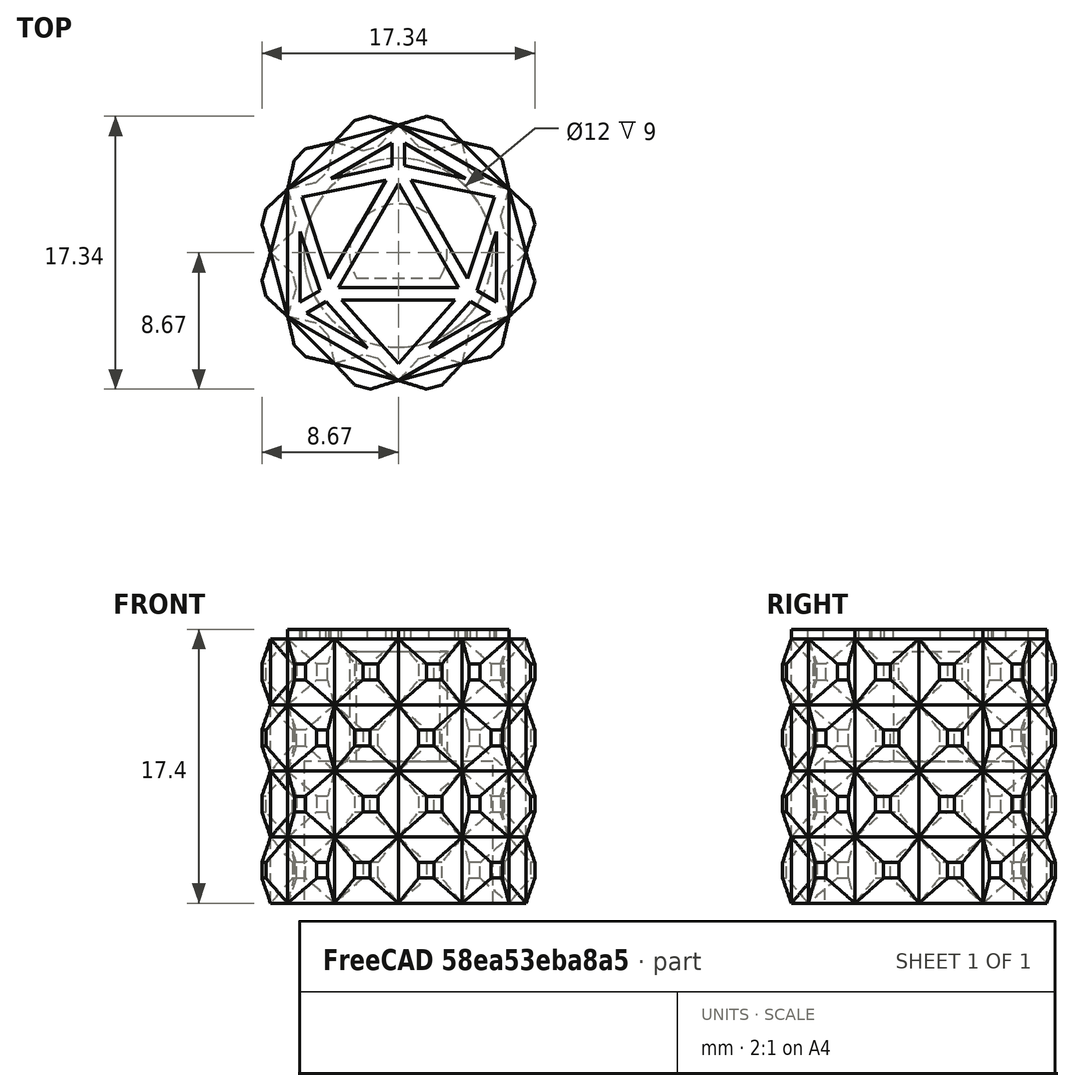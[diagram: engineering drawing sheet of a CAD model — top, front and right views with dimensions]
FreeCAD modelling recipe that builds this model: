
FCSTD DOCUMENT  (FreeCAD 1.0R38641 +678 (Git))
Label: knob
License: All rights reserved
LicenseURL: https://en.wikipedia.org/wiki/All_rights_reserved
objects: Sketcher::SketchObject×18, PartDesign::Pad×5, PartDesign::Pocket×5, PartDesign::AdditiveLoft×2, PartDesign::SubtractiveLoft×2, PartDesign::PolarPattern×1, PartDesign::LinearPattern×1, PartDesign::MultiTransform×1, PartDesign::Body×1, Mesh::Feature×1
note: 85 computed .brp shape members not serialized (recipe doc carries the construction recipe); baked Part::Feature solids carry a one-line shape summary decoded from their .brp

FEATURE [Sketcher::SketchObject] Sketch
  ArcFitTolerance = 0
  AttachmentSupport = -> [XY_Plane]
  FullyConstrained = true
  MakeInternals = false
  MapMode = 5
  sketch-geometry (5):
    g0: LineSegment StartX=0 StartY=0 StartZ=0 EndX=0 EndY=-8.11378 EndZ=0
    g1: LineSegment [constr] StartX=0 StartY=0 StartZ=0 EndX=4.05689 EndY=-7.02674 EndZ=0
    g2: LineSegment StartX=0 StartY=-8.11378 StartZ=0 EndX=4.05689 EndY=-7.02674 EndZ=0
    g3: LineSegment StartX=0 StartY=0 StartZ=0 EndX=7.02674 EndY=-4.05689 EndZ=0
    g4: LineSegment StartX=4.05689 StartY=-7.02674 StartZ=0 EndX=7.02674 EndY=-4.05689 EndZ=0
  constraints (13):
    c: Coincident(g0,g-1)
    c: PointOnObject(g0,g-2)
    c: Coincident(g1,g0)
    c: Equal(g0,g1)
    c: Coincident(g2,g0)
    c: Coincident(g1,g2)
    c: Angle(g0,g1) = 0.523599
    c: Coincident(g3,g0)
    c: Coincident(g4,g1)
    c: Coincident(g4,g3)
    c: Equal(g1,g3)
    c: Angle(g1,g3) = 0.523599
    c: Distance(g2) = 4.2
FEATURE [PartDesign::Pad] Pad
  Direction = (0,0,1)
  Length = 8.4
  Length2 = 10
  Profile = -> Sketch
  ReferenceAxis = -> Sketch [N_Axis]
  Suppressed = false
  Type = 0
FEATURE [Sketcher::SketchObject] Sketch001
  ArcFitTolerance = 0
  AttachmentSupport = -> [Pad]
  ExternalGeometry = -> [Pad]
  FullyConstrained = true
  MakeInternals = false
  MapMode = 5
  Placement = pos=(2.02844,-7.57026,0) rot=(0.983106,0.129428,0.129428;1.58783rad)
  sketch-geometry (4):
    g0: LineSegment StartX=-0.5 StartY=6.8 StartZ=0 EndX=0.5 EndY=6.8 EndZ=0
    g1: LineSegment StartX=0.5 StartY=6.8 StartZ=0 EndX=0.5 EndY=5.8 EndZ=0
    g2: LineSegment StartX=0.5 StartY=5.8 StartZ=0 EndX=-0.5 EndY=5.8 EndZ=0
    g3: LineSegment StartX=-0.5 StartY=5.8 StartZ=0 EndX=-0.5 EndY=6.8 EndZ=0
  constraints (12):
    c: Coincident(g0,g1)
    c: Coincident(g1,g2)
    c: Coincident(g2,g3)
    c: Coincident(g3,g0)
    c: Horizontal(g0)
    c: Horizontal(g2)
    c: Vertical(g1)
    c: Vertical(g3)
    c: DistanceX(g-4,g0) = 1.6
    c: DistanceX(g0,g-5) = 1.6
    c: DistanceY(g0,g-4) = 1.6
    c: DistanceY(g3,g3) = 1
FEATURE [PartDesign::Pad] Pad001
  BaseFeature = -> Pad
  Direction = (0.258819,-0.965926,0)
  Length = 1
  Length2 = 10
  Profile = -> Sketch001
  ReferenceAxis = -> Sketch001 [N_Axis]
  Suppressed = false
  Type = 0
FEATURE [Sketcher::SketchObject] Sketch002
  ArcFitTolerance = 0
  AttachmentSupport = -> [Pad001]
  ExternalGeometry = -> [Pad001]
  FullyConstrained = true
  MakeInternals = false
  MapMode = 5
  Placement = pos=(2.02844,-7.57026,0) rot=(0.983106,0.129428,0.129428;1.58783rad)
  sketch-geometry (4):
    g0: LineSegment StartX=-2.1 StartY=8.4 StartZ=0 EndX=2.1 EndY=8.4 EndZ=0
    g1: LineSegment StartX=2.1 StartY=8.4 StartZ=0 EndX=2.1 EndY=4.2 EndZ=0
    g2: LineSegment StartX=2.1 StartY=4.2 StartZ=0 EndX=-2.1 EndY=4.2 EndZ=0
    g3: LineSegment StartX=-2.1 StartY=4.2 StartZ=0 EndX=-2.1 EndY=8.4 EndZ=0
  constraints (10):
    c: Coincident(g0,g1)
    c: Coincident(g1,g2)
    c: Coincident(g2,g3)
    c: Coincident(g3,g0)
    c: Horizontal(g2)
    c: Vertical(g1)
    c: Vertical(g3)
    c: DistanceY(g3,g3) = 4.2
    c: Coincident(g0,g-5)
    c: Coincident(g0,g-4)
FEATURE [Sketcher::SketchObject] Sketch003
  ArcFitTolerance = 0
  AttachmentSupport = -> [Pad001]
  ExternalGeometry = -> [Pad001]
  FullyConstrained = true
  MakeInternals = false
  MapMode = 5
  Placement = pos=(2.28726,-8.53618,0) rot=(0.983106,0.129428,0.129428;1.58783rad)
  sketch-geometry (4):
    g0: LineSegment StartX=-0.5 StartY=6.8 StartZ=0 EndX=0.5 EndY=6.8 EndZ=0
    g1: LineSegment StartX=0.5 StartY=6.8 StartZ=0 EndX=0.5 EndY=5.8 EndZ=0
    g2: LineSegment StartX=0.5 StartY=5.8 StartZ=0 EndX=-0.5 EndY=5.8 EndZ=0
    g3: LineSegment StartX=-0.5 StartY=5.8 StartZ=0 EndX=-0.5 EndY=6.8 EndZ=0
  constraints (10):
    c: Coincident(g0,g1)
    c: Coincident(g1,g2)
    c: Coincident(g2,g3)
    c: Coincident(g3,g0)
    c: Horizontal(g0)
    c: Horizontal(g2)
    c: Vertical(g1)
    c: Vertical(g3)
    c: Coincident(g0,g-6)
    c: Coincident(g1,g-5)
FEATURE [PartDesign::AdditiveLoft] AdditiveLoft
  BaseFeature = -> Pad001
  Closed = false
  Profile = -> Sketch002
  Ruled = false
  Sections = -> [Sketch003]
  Suppressed = false
FEATURE [Sketcher::SketchObject] Sketch004
  ArcFitTolerance = 0
  AttachmentSupport = -> [AdditiveLoft]
  ExternalGeometry = -> [AdditiveLoft]
  FullyConstrained = true
  MakeInternals = false
  MapMode = 5
  Placement = pos=(2.02844,-7.57026,0) rot=(0.983106,0.129428,0.129428;1.58783rad)
  sketch-geometry (4):
    g0: LineSegment StartX=-0.5 StartY=2.6 StartZ=0 EndX=0.5 EndY=2.6 EndZ=0
    g1: LineSegment StartX=0.5 StartY=2.6 StartZ=0 EndX=0.5 EndY=1.6 EndZ=0
    g2: LineSegment StartX=0.5 StartY=1.6 StartZ=0 EndX=-0.5 EndY=1.6 EndZ=0
    g3: LineSegment StartX=-0.5 StartY=1.6 StartZ=0 EndX=-0.5 EndY=2.6 EndZ=0
  constraints (12):
    c: Coincident(g0,g1)
    c: Coincident(g1,g2)
    c: Coincident(g2,g3)
    c: Coincident(g3,g0)
    c: Horizontal(g0)
    c: Horizontal(g2)
    c: Vertical(g1)
    c: Vertical(g3)
    c: DistanceX(g-3,g2) = 1.6
    c: DistanceY(g-3,g2) = 1.6
    c: DistanceX(g1,g-4) = 1.6
    c: DistanceY(g3,g3) = 1
FEATURE [PartDesign::Pocket] Pocket
  BaseFeature = -> AdditiveLoft
  Direction = (-0.258819,0.965926,0)
  Length = 1
  Length2 = 5
  Profile = -> Sketch004
  ReferenceAxis = -> Sketch004 [N_Axis]
  Suppressed = false
  Type = 0
FEATURE [Sketcher::SketchObject] Sketch005
  ArcFitTolerance = 0
  AttachmentSupport = -> [Pocket]
  ExternalGeometry = -> [Pocket]
  FullyConstrained = true
  MakeInternals = false
  MapMode = 5
  Placement = pos=(2.02844,-7.57026,0) rot=(0.983106,0.129428,0.129428;1.58783rad)
  sketch-geometry (4):
    g0: LineSegment StartX=-2.1 StartY=4.2 StartZ=0 EndX=2.1 EndY=4.2 EndZ=0
    g1: LineSegment StartX=2.1 StartY=4.2 StartZ=0 EndX=2.1 EndY=0 EndZ=0
    g2: LineSegment StartX=2.1 StartY=0 StartZ=0 EndX=-2.1 EndY=0 EndZ=0
    g3: LineSegment StartX=-2.1 StartY=0 StartZ=0 EndX=-2.1 EndY=4.2 EndZ=0
  constraints (10):
    c: Coincident(g0,g1)
    c: Coincident(g1,g2)
    c: Coincident(g2,g3)
    c: Coincident(g3,g0)
    c: Horizontal(g0)
    c: Horizontal(g2)
    c: Vertical(g1)
    c: Vertical(g3)
    c: Coincident(g0,g-4)
    c: Coincident(g1,g-6)
FEATURE [Sketcher::SketchObject] Sketch006
  ArcFitTolerance = 0
  AttachmentSupport = -> [Pocket]
  ExternalGeometry = -> [Pocket]
  FullyConstrained = true
  MakeInternals = false
  MapMode = 5
  Placement = pos=(1.76963,-6.60433,0) rot=(0.983106,0.129428,0.129428;1.58783rad)
  sketch-geometry (4):
    g0: LineSegment StartX=-0.5 StartY=2.6 StartZ=0 EndX=0.5 EndY=2.6 EndZ=0
    g1: LineSegment StartX=0.5 StartY=2.6 StartZ=0 EndX=0.5 EndY=1.6 EndZ=0
    g2: LineSegment StartX=0.5 StartY=1.6 StartZ=0 EndX=-0.5 EndY=1.6 EndZ=0
    g3: LineSegment StartX=-0.5 StartY=1.6 StartZ=0 EndX=-0.5 EndY=2.6 EndZ=0
  constraints (10):
    c: Coincident(g0,g1)
    c: Coincident(g1,g2)
    c: Coincident(g2,g3)
    c: Coincident(g3,g0)
    c: Horizontal(g0)
    c: Horizontal(g2)
    c: Vertical(g1)
    c: Vertical(g3)
    c: Coincident(g0,g-4)
    c: Coincident(g1,g-6)
FEATURE [PartDesign::SubtractiveLoft] SubtractiveLoft
  BaseFeature = -> Pocket
  Closed = false
  Profile = -> Sketch006
  Ruled = false
  Sections = -> [Sketch005]
  Suppressed = false
FEATURE [Sketcher::SketchObject] Sketch007
  ArcFitTolerance = 0
  AttachmentSupport = -> [SubtractiveLoft]
  ExternalGeometry = -> [SubtractiveLoft]
  FullyConstrained = true
  MakeInternals = false
  MapMode = 5
  Placement = pos=(5.54181,-5.54181,0) rot=(0.862856,0.357407,0.357407;1.71777rad)
  sketch-geometry (4):
    g0: LineSegment StartX=-0.5 StartY=6.8 StartZ=0 EndX=0.5 EndY=6.8 EndZ=0
    g1: LineSegment StartX=0.5 StartY=6.8 StartZ=0 EndX=0.5 EndY=5.8 EndZ=0
    g2: LineSegment StartX=0.5 StartY=5.8 StartZ=0 EndX=-0.5 EndY=5.8 EndZ=0
    g3: LineSegment StartX=-0.5 StartY=5.8 StartZ=0 EndX=-0.5 EndY=6.8 EndZ=0
  constraints (12):
    c: Coincident(g0,g1)
    c: Coincident(g1,g2)
    c: Coincident(g2,g3)
    c: Coincident(g3,g0)
    c: Horizontal(g0)
    c: Horizontal(g2)
    c: Vertical(g1)
    c: Vertical(g3)
    c: DistanceX(g-4,g0) = 1.6
    c: DistanceX(g0,g-3) = 1.6
    c: DistanceY(g0,g-3) = 1.6
    c: DistanceY(g1,g1) = 1
FEATURE [PartDesign::Pocket] Pocket001
  BaseFeature = -> SubtractiveLoft
  Direction = (-0.707107,0.707107,1e-16)
  Length = 1
  Length2 = 5
  Profile = -> Sketch007
  ReferenceAxis = -> Sketch007 [N_Axis]
  Suppressed = false
  Type = 0
FEATURE [Sketcher::SketchObject] Sketch008
  ArcFitTolerance = 0
  AttachmentSupport = -> [Pocket001]
  ExternalGeometry = -> [Pocket001]
  FullyConstrained = true
  MakeInternals = false
  MapMode = 5
  Placement = pos=(5.54181,-5.54181,0) rot=(0.862856,0.357407,0.357407;1.71777rad)
  sketch-geometry (4):
    g0: LineSegment StartX=-2.1 StartY=8.4 StartZ=0 EndX=2.1 EndY=8.4 EndZ=0
    g1: LineSegment StartX=2.1 StartY=8.4 StartZ=0 EndX=2.1 EndY=4.2 EndZ=0
    g2: LineSegment StartX=2.1 StartY=4.2 StartZ=0 EndX=-2.1 EndY=4.2 EndZ=0
    g3: LineSegment StartX=-2.1 StartY=4.2 StartZ=0 EndX=-2.1 EndY=8.4 EndZ=0
  constraints (9):
    c: Coincident(g0,g1)
    c: Coincident(g1,g2)
    c: Coincident(g2,g3)
    c: Coincident(g3,g0)
    c: Horizontal(g2)
    c: Vertical(g1)
    c: Coincident(g0,g-4)
    c: Coincident(g2,g-3)
    c: Coincident(g-4,g0)
FEATURE [Sketcher::SketchObject] Sketch009
  ArcFitTolerance = 0
  AttachmentSupport = -> [Pocket001]
  ExternalGeometry = -> [Pocket001]
  FullyConstrained = true
  MakeInternals = false
  MapMode = 5
  Placement = pos=(4.83471,-4.83471,0) rot=(0.862856,0.357407,0.357407;1.71777rad)
  sketch-geometry (4):
    g0: LineSegment StartX=-0.5 StartY=6.8 StartZ=0 EndX=0.5 EndY=6.8 EndZ=0
    g1: LineSegment StartX=0.5 StartY=6.8 StartZ=0 EndX=0.5 EndY=5.8 EndZ=0
    g2: LineSegment StartX=0.5 StartY=5.8 StartZ=0 EndX=-0.5 EndY=5.8 EndZ=0
    g3: LineSegment StartX=-0.5 StartY=5.8 StartZ=0 EndX=-0.5 EndY=6.8 EndZ=0
  constraints (10):
    c: Coincident(g0,g1)
    c: Coincident(g1,g2)
    c: Coincident(g2,g3)
    c: Coincident(g3,g0)
    c: Horizontal(g0)
    c: Horizontal(g2)
    c: Vertical(g1)
    c: Vertical(g3)
    c: Coincident(g0,g-4)
    c: Coincident(g1,g-6)
FEATURE [PartDesign::SubtractiveLoft] SubtractiveLoft001
  BaseFeature = -> Pocket001
  Closed = false
  Profile = -> Sketch008
  Ruled = false
  Sections = -> [Sketch009]
  Suppressed = false
FEATURE [Sketcher::SketchObject] Sketch010
  ArcFitTolerance = 0
  AttachmentSupport = -> [SubtractiveLoft001]
  ExternalGeometry = -> [SubtractiveLoft001]
  FullyConstrained = true
  MakeInternals = false
  MapMode = 5
  Placement = pos=(5.54181,-5.54181,0) rot=(0.862856,0.357407,0.357407;1.71777rad)
  sketch-geometry (4):
    g0: LineSegment StartX=-0.5 StartY=2.6 StartZ=0 EndX=0.5 EndY=2.6 EndZ=0
    g1: LineSegment StartX=0.5 StartY=2.6 StartZ=0 EndX=0.5 EndY=1.6 EndZ=0
    g2: LineSegment StartX=0.5 StartY=1.6 StartZ=0 EndX=-0.5 EndY=1.6 EndZ=0
    g3: LineSegment StartX=-0.5 StartY=1.6 StartZ=0 EndX=-0.5 EndY=2.6 EndZ=0
  constraints (12):
    c: Coincident(g0,g1)
    c: Coincident(g1,g2)
    c: Coincident(g2,g3)
    c: Coincident(g3,g0)
    c: Horizontal(g0)
    c: Horizontal(g2)
    c: Vertical(g1)
    c: Vertical(g3)
    c: DistanceX(g-6,g2) = 1.6
    c: DistanceX(g1,g-6) = 1.6
    c: DistanceY(g-6,g1) = 1.6
    c: DistanceY(g1,g1) = 1
FEATURE [PartDesign::Pad] Pad002
  BaseFeature = -> SubtractiveLoft001
  Direction = (0.707107,-0.707107,-1e-16)
  Length = 1
  Length2 = 10
  Profile = -> Sketch010
  ReferenceAxis = -> Sketch010 [N_Axis]
  Suppressed = false
  Type = 0
FEATURE [Sketcher::SketchObject] Sketch011
  ArcFitTolerance = 0
  AttachmentSupport = -> [Pad002]
  ExternalGeometry = -> [Pad002]
  FullyConstrained = true
  MakeInternals = false
  MapMode = 5
  Placement = pos=(5.54181,-5.54181,0) rot=(0.862856,0.357407,0.357407;1.71777rad)
  sketch-geometry (4):
    g0: LineSegment StartX=-2.1 StartY=4.2 StartZ=0 EndX=2.1 EndY=4.2 EndZ=0
    g1: LineSegment StartX=2.1 StartY=4.2 StartZ=0 EndX=2.1 EndY=0 EndZ=0
    g2: LineSegment StartX=2.1 StartY=0 StartZ=0 EndX=-2.1 EndY=0 EndZ=0
    g3: LineSegment StartX=-2.1 StartY=0 StartZ=0 EndX=-2.1 EndY=4.2 EndZ=0
  constraints (10):
    c: Coincident(g0,g1)
    c: Coincident(g1,g2)
    c: Coincident(g2,g3)
    c: Coincident(g3,g0)
    c: Horizontal(g0)
    c: Horizontal(g2)
    c: Vertical(g1)
    c: Vertical(g3)
    c: Coincident(g0,g-4)
    c: Coincident(g1,g-6)
FEATURE [Sketcher::SketchObject] Sketch012
  ArcFitTolerance = 0
  AttachmentSupport = -> [Pad002]
  ExternalGeometry = -> [Pad002]
  FullyConstrained = true
  MakeInternals = false
  MapMode = 5
  Placement = pos=(6.24892,-6.24892,-2.7e-15) rot=(0.862856,0.357407,0.357407;1.71777rad)
  sketch-geometry (4):
    g0: LineSegment StartX=-0.5 StartY=2.6 StartZ=0 EndX=0.5 EndY=2.6 EndZ=0
    g1: LineSegment StartX=0.5 StartY=2.6 StartZ=0 EndX=0.5 EndY=1.6 EndZ=0
    g2: LineSegment StartX=0.5 StartY=1.6 StartZ=0 EndX=-0.5 EndY=1.6 EndZ=0
    g3: LineSegment StartX=-0.5 StartY=1.6 StartZ=0 EndX=-0.5 EndY=2.6 EndZ=0
  constraints (10):
    c: Coincident(g0,g1)
    c: Coincident(g1,g2)
    c: Coincident(g2,g3)
    c: Coincident(g3,g0)
    c: Horizontal(g0)
    c: Horizontal(g2)
    c: Vertical(g1)
    c: Vertical(g3)
    c: Coincident(g0,g-4)
    c: Coincident(g1,g-6)
FEATURE [PartDesign::AdditiveLoft] AdditiveLoft001
  BaseFeature = -> Pad002
  Closed = false
  Profile = -> Sketch011
  Ruled = false
  Sections = -> [Sketch012]
  Suppressed = false
FEATURE [PartDesign::PolarPattern] PolarPattern
  Angle = 360
  Axis = -> Sketch [N_Axis]
  Mode = 0
  Occurrences = 6
  Offset = 120
  Suppressed = false
  TransformMode = 0
FEATURE [PartDesign::LinearPattern] LinearPattern
  Direction = -> Z_Axis
  Length = 8.4
  Mode = 0
  Occurrences = 2
  Offset = 8.4
  Suppressed = false
  TransformMode = 0
FEATURE [PartDesign::MultiTransform] MultiTransform
  BaseFeature = -> AdditiveLoft001
  Originals = -> [Pad,Pad001,AdditiveLoft,Pocket,SubtractiveLoft,Pocket001,SubtractiveLoft001,Pad002,AdditiveLoft001]
  Suppressed = false
  TransformMode = 0
  Transformations = -> [PolarPattern,LinearPattern]
FEATURE [Sketcher::SketchObject] Sketch013
  ArcFitTolerance = 0
  AttachmentSupport = -> [MultiTransform]
  FullyConstrained = true
  MakeInternals = false
  MapMode = 5
  Placement = pos=(0,0,0) rot=(1,0,0;3.14159rad)
  sketch-geometry (1):
    g0: Circle CenterX=0 CenterY=0 CenterZ=0 NormalX=0 NormalY=0 NormalZ=1 AngleXU=0 Radius=6
  constraints (2):
    c: Coincident(g0,g-1)
    c: Diameter(g0) = 12
FEATURE [PartDesign::Pocket] Pocket002
  BaseFeature = -> MultiTransform
  Direction = (0,0,1)
  Length = 9
  Length2 = 5
  Profile = -> Sketch013
  ReferenceAxis = -> Sketch013 [N_Axis]
  Suppressed = false
  Type = 0
FEATURE [Sketcher::SketchObject] Sketch014
  ArcFitTolerance = 0
  AttachmentSupport = -> [Pocket002]
  FullyConstrained = true
  MakeInternals = false
  MapMode = 5
  Placement = pos=(0,0,9) rot=(1,0,0;3.14159rad)
  sketch-geometry (2):
    g0: LineSegment StartX=-2.65518 StartY=1.6 StartZ=0 EndX=2.65518 EndY=1.6 EndZ=0
    g1: ArcOfCircle CenterX=0 CenterY=0 CenterZ=0 NormalX=0 NormalY=0 NormalZ=1 AngleXU=0 Radius=3.1 StartAngle=2.59927 EndAngle=6.82551
  constraints (6):
    c: Horizontal(g0)
    c: Coincident(g1,g-1)
    c: Coincident(g1,g0)
    c: Coincident(g1,g0)
    c: Radius(g1) = 3.1
    c: DistanceY(g1,g0) = 1.6
FEATURE [PartDesign::Pocket] Pocket003
  BaseFeature = -> Pocket002
  Direction = (0,0,1)
  Length = 7
  Length2 = 5
  Profile = -> Sketch014
  ReferenceAxis = -> Sketch014 [N_Axis]
  Suppressed = false
  Type = 0
FEATURE [Sketcher::SketchObject] Sketch015
  ArcFitTolerance = 0
  AttachmentSupport = -> [Pocket003]
  ExternalGeometry = -> [Pocket003]
  FullyConstrained = true
  MakeInternals = false
  MapMode = 5
  Placement = pos=(0,0,16.8) rot=(0,0,1;0rad)
  sketch-geometry (54):
    g0: LineSegment [constr] StartX=0 StartY=5.19615 StartZ=0 EndX=-4.5 EndY=-2.59808 EndZ=0
    g1: LineSegment [constr] StartX=-4.5 StartY=-2.59808 StartZ=0 EndX=4.5 EndY=-2.59808 EndZ=0
    g2: LineSegment [constr] StartX=4.5 StartY=-2.59808 StartZ=0 EndX=0 EndY=5.19615 EndZ=0
    g3: LineSegment [constr] StartX=4.4e-15 StartY=8.11378 StartZ=0 EndX=0 EndY=5.19615 EndZ=0
    g4: LineSegment StartX=-7.02674 StartY=4.05689 StartZ=0 EndX=4.4e-15 EndY=8.11378 EndZ=0
    g5: LineSegment StartX=-7.02674 StartY=4.05689 StartZ=0 EndX=-7.02674 EndY=-4.05689 EndZ=0
    g6: LineSegment [constr] StartX=4.5 StartY=-2.59808 StartZ=0 EndX=7.02674 EndY=-4.05689 EndZ=0
    g7: LineSegment [constr] StartX=-4.5 StartY=-2.59808 StartZ=0 EndX=-7.02674 EndY=-4.05689 EndZ=0
    g8: LineSegment [constr] StartX=-6.62674 StartY=3.82595 StartZ=0 EndX=3.6e-15 EndY=7.6519 EndZ=0
    g9: LineSegment [constr] StartX=3.6e-15 StartY=7.6519 StartZ=0 EndX=6.62674 EndY=3.82595 EndZ=0
    g10: LineSegment [constr] StartX=6.62674 StartY=3.82595 StartZ=0 EndX=6.62674 EndY=-3.82595 EndZ=0
    g11: LineSegment [constr] StartX=6.62674 StartY=-3.82595 StartZ=0 EndX=9e-16 EndY=-7.6519 EndZ=0
    g12: LineSegment [constr] StartX=9e-16 StartY=-7.6519 StartZ=0 EndX=-6.62674 EndY=-3.82595 EndZ=0
    g13: LineSegment [constr] StartX=-6.62674 StartY=-3.82595 StartZ=0 EndX=-6.62674 EndY=3.82595 EndZ=0
    g14: LineSegment StartX=-7.02674 StartY=-4.05689 StartZ=0 EndX=9e-16 EndY=-8.11378 EndZ=0
    g15: LineSegment StartX=9e-16 StartY=-8.11378 StartZ=0 EndX=7.02674 EndY=-4.05689 EndZ=0
    g16: LineSegment StartX=4.4e-15 StartY=8.11378 StartZ=0 EndX=7.02674 EndY=4.05689 EndZ=0
    g17: LineSegment StartX=7.02674 StartY=4.05689 StartZ=0 EndX=7.02674 EndY=-4.05689 EndZ=0
    g18: LineSegment [constr] StartX=-4.5 StartY=-2.59808 StartZ=0 EndX=-6.62674 EndY=3.82595 EndZ=0
    g19: LineSegment [constr] StartX=-6.62674 StartY=3.82595 StartZ=0 EndX=0 EndY=5.19615 EndZ=0
    g20: LineSegment [constr] StartX=0 StartY=5.19615 StartZ=0 EndX=6.62674 EndY=3.82595 EndZ=0
    g21: LineSegment [constr] StartX=6.62674 StartY=3.82595 StartZ=0 EndX=4.5 EndY=-2.59808 EndZ=0
    g22: LineSegment [constr] StartX=-4.5 StartY=-2.59808 StartZ=0 EndX=9e-16 EndY=-7.6519 EndZ=0
    g23: LineSegment [constr] StartX=4.5 StartY=-2.59808 StartZ=0 EndX=9e-16 EndY=-7.6519 EndZ=0
    g24: LineSegment StartX=-4.27815 StartY=4.72002 StartZ=0 EndX=-0.4 EndY=6.95908 EndZ=0
    g25: LineSegment StartX=-0.4 StartY=6.95908 StartZ=0 EndX=-0.4 EndY=5.52191 EndZ=0
    g26: LineSegment StartX=-0.4 StartY=5.52191 StartZ=0 EndX=-4.27815 EndY=4.72002 EndZ=0
    g27: LineSegment StartX=0.4 StartY=6.95908 StartZ=0 EndX=0.4 EndY=5.52191 EndZ=0
    g28: LineSegment StartX=0.4 StartY=5.52191 StartZ=0 EndX=4.27815 EndY=4.72002 EndZ=0
    g29: LineSegment StartX=4.27815 StartY=4.72002 StartZ=0 EndX=0.4 EndY=6.95908 EndZ=0
    g30: LineSegment StartX=-0.792287 StartY=4.62387 StartZ=0 EndX=-4.40053 EndY=-1.62579 EndZ=0
    g31: LineSegment StartX=-4.40053 StartY=-1.62579 StartZ=0 EndX=-6.10582 EndY=3.5252 EndZ=0
    g32: LineSegment StartX=-6.10582 StartY=3.5252 StartZ=0 EndX=-0.792287 EndY=4.62387 EndZ=0
    g33: LineSegment StartX=0.792287 StartY=4.62387 StartZ=0 EndX=6.10582 EndY=3.5252 EndZ=0
    g34: LineSegment StartX=6.10582 StartY=3.5252 StartZ=0 EndX=4.40053 EndY=-1.62579 EndZ=0
    g35: LineSegment StartX=4.40053 StartY=-1.62579 StartZ=0 EndX=0.792287 EndY=4.62387 EndZ=0
    g36: LineSegment StartX=0 StartY=4.39615 StartZ=0 EndX=-3.80718 EndY=-2.19808 EndZ=0
    g37: LineSegment StartX=-3.80718 StartY=-2.19808 StartZ=0 EndX=3.80718 EndY=-2.19808 EndZ=0
    g38: LineSegment StartX=3.80718 StartY=-2.19808 StartZ=0 EndX=0 EndY=4.39615 EndZ=0
    g39: LineSegment StartX=-3.60825 StartY=-2.99808 StartZ=0 EndX=3.60825 EndY=-2.99808 EndZ=0
    g40: LineSegment StartX=3.60825 StartY=-2.99808 StartZ=0 EndX=9e-16 EndY=-7.05039 EndZ=0
    g41: LineSegment StartX=9e-16 StartY=-7.05039 StartZ=0 EndX=-3.60825 EndY=-2.99808 EndZ=0
    g42: LineSegment StartX=-6.22674 StartY=1.34498 StartZ=0 EndX=-4.98211 EndY=-2.41454 EndZ=0
    g43: LineSegment StartX=-4.98211 StartY=-2.41454 StartZ=0 EndX=-6.22674 EndY=-3.13313 EndZ=0
    g44: LineSegment StartX=-6.22674 StartY=-3.13313 StartZ=0 EndX=-6.22674 EndY=1.34498 EndZ=0
    g45: LineSegment StartX=4.98211 StartY=-2.41454 StartZ=0 EndX=6.22674 EndY=-3.13313 EndZ=0
    g46: LineSegment StartX=6.22674 StartY=-3.13313 StartZ=0 EndX=6.22674 EndY=1.34498 EndZ=0
    g47: LineSegment StartX=6.22674 StartY=1.34498 StartZ=0 EndX=4.98211 EndY=-2.41454 EndZ=0
    g48: LineSegment StartX=5.82674 StartY=-3.82595 StartZ=0 EndX=1.94858 EndY=-6.065 EndZ=0
    g49: LineSegment StartX=1.94858 StartY=-6.065 StartZ=0 EndX=4.58211 EndY=-3.10736 EndZ=0
    g50: LineSegment StartX=4.58211 StartY=-3.10736 StartZ=0 EndX=5.82674 EndY=-3.82595 EndZ=0
    g51: LineSegment StartX=-5.82674 StartY=-3.82595 StartZ=0 EndX=-4.58211 EndY=-3.10736 EndZ=0
    g52: LineSegment StartX=-4.58211 StartY=-3.10736 StartZ=0 EndX=-1.94858 EndY=-6.065 EndZ=0
    g53: LineSegment StartX=-1.94858 StartY=-6.065 StartZ=0 EndX=-5.82674 EndY=-3.82595 EndZ=0
  constraints (147):
    c: Coincident(g1,g0)
    c: Coincident(g2,g1)
    c: Coincident(g2,g0)
    c: PointOnObject(g0,g-2)
    c: Equal(g0,g1)
    c: Equal(g1,g2)
    c: PointOnObject(g0,g-4)
    c: DistanceX(g1,g1) = 9
    c: Coincident(g3,g-8)
    c: Coincident(g3,g0)
    c: Coincident(g4,g-3)
    c: Coincident(g4,g3)
    c: Coincident(g5,g4)
    c: Coincident(g5,g-4)
    c: Coincident(g6,g1)
    c: Coincident(g7,g0)
    c: Coincident(g7,g5)
    c: PointOnObject(g1,g-6)
    c: PointOnObject(g8,g-3)
    c: PointOnObject(g8,g3)
    c: Coincident(g9,g8)
    c: PointOnObject(g9,g-7)
    c: Coincident(g10,g9)
    c: PointOnObject(g10,g6)
    c: Coincident(g11,g10)
    c: PointOnObject(g11,g-5)
    c: Coincident(g12,g11)
    c: PointOnObject(g12,g7)
    c: Coincident(g13,g12)
    c: Coincident(g13,g8)
    c: Parallel(g8,g4)
    c: Coincident(g14,g5)
    c: Coincident(g14,g-5)
    c: Coincident(g15,g14)
    c: Coincident(g15,g6)
    c: Coincident(g6,g-6)
    c: Coincident(g16,g3)
    c: Coincident(g16,g-7)
    c: Coincident(g17,g16)
    c: Coincident(g17,g6)
    c: Parallel(g9,g16)
    c: Parallel(g10,g17)
    c: Parallel(g11,g15)
    c: Parallel(g12,g14)
    c: Distance(g8,g4) = 0.4
    c: Coincident(g18,g0)
    c: Coincident(g18,g8)
    c: Coincident(g19,g8)
    c: Coincident(g19,g0)
    c: Coincident(g20,g0)
    c: Coincident(g20,g9)
    c: Coincident(g21,g9)
    c: Coincident(g21,g1)
    c: Coincident(g22,g0)
    c: Coincident(g22,g11)
    c: Coincident(g23,g1)
    c: Coincident(g23,g11)
    c: Coincident(g25,g24)
    c: Coincident(g26,g25)
    c: Coincident(g26,g24)
    c: Coincident(g28,g27)
    c: Coincident(g29,g28)
    c: Coincident(g29,g27)
    c: Coincident(g31,g30)
    c: Coincident(g32,g31)
    c: Coincident(g32,g30)
    c: Coincident(g34,g33)
    c: Coincident(g35,g34)
    c: Coincident(g35,g33)
    c: Coincident(g37,g36)
    c: Coincident(g38,g37)
    c: Coincident(g38,g36)
    c: Coincident(g40,g39)
    c: Coincident(g41,g40)
    c: Coincident(g41,g39)
    c: Coincident(g43,g42)
    c: Coincident(g44,g43)
    c: Coincident(g44,g42)
    c: Coincident(g46,g45)
    c: Coincident(g47,g46)
    c: Coincident(g47,g45)
    c: Coincident(g49,g48)
    c: Coincident(g50,g49)
    c: Coincident(g50,g48)
    c: Coincident(g52,g51)
    c: Coincident(g53,g52)
    c: Coincident(g53,g51)
    c: Parallel(g25,g27)
    c: Parallel(g27,g3)
    c: Parallel(g32,g19)
    c: Parallel(g33,g20)
    c: Parallel(g38,g2)
    c: Parallel(g36,g0)
    c: Parallel(g37,g1)
    c: Parallel(g21,g34)
    c: Parallel(g47,g21)
    c: Parallel(g46,g10)
    c: Parallel(g45,g6)
    c: Parallel(g50,g6)
    c: Parallel(g48,g11)
    c: Parallel(g49,g23)
    c: Parallel(g40,g23)
    c: Parallel(g39,g1)
    c: Parallel(g41,g22)
    c: Parallel(g52,g22)
    c: Parallel(g53,g12)
    c: Parallel(g51,g7)
    c: Parallel(g43,g7)
    c: Parallel(g44,g13)
    c: Parallel(g42,g18)
    c: Parallel(g8,g24)
    c: Distance(g24,g8) = 0.4
    c: Parallel(g26,g19)
    c: Distance(g19,g26) = 0.4
    c: Distance(g25,g3) = 0.4
    c: Distance(g27,g3) = 0.4
    c: Parallel(g29,g9)
    c: Distance(g9,g29) = 0.4
    c: Parallel(g28,g20)
    c: Distance(g20,g28) = 0.4
    c: Parallel(g35,g2)
    c: Distance(g35,g2) = 0.4
    c: Distance(g33,g20) = 0.4
    c: Distance(g21,g34) = 0.4
    c: Parallel(g30,g0)
    c: Distance(g0,g30) = 0.4
    c: Distance(g32,g19) = 0.4
    c: Parallel(g31,g18)
    c: Distance(g31,g18) = 0.4
    c: Distance(g13,g44) = 0.4
    c: Distance(g18,g42) = 0.4
    c: Distance(g7,g43) = 0.4
    c: Distance(g1,g37) = 0.4
    c: Distance(g2,g38) = 0.4
    c: Distance(g36,g0) = 0.4
    c: Distance(g10,g46) = 0.4
    c: Distance(g21,g47) = 0.4
    c: Distance(g6,g45) = 0.4
    c: Distance(g11,g48) = 0.4
    c: Distance(g6,g50) = 0.4
    c: Distance(g49,g23) = 0.4
    c: Distance(g39,g1) = 0.4
    c: Distance(g23,g40) = 0.4
    c: Distance(g22,g41) = 0.4
    c: Distance(g22,g52) = 0.4
    c: Distance(g12,g53) = 0.4
    c: Distance(g7,g51) = 0.4
FEATURE [PartDesign::Pad] Pad003
  BaseFeature = -> Pocket003
  Direction = (0,0,1)
  Length = 0.6
  Length2 = 10
  Profile = -> Sketch015
  ReferenceAxis = -> Sketch015 [N_Axis]
  Suppressed = false
  Type = 0
FEATURE [Sketcher::SketchObject] Sketch016
  ArcFitTolerance = 0
  AttachmentSupport = -> [Pad003]
  FullyConstrained = true
  MakeInternals = false
  MapMode = 5
  Placement = pos=(0,0,0) rot=(1,0,0;3.14159rad)
  sketch-geometry (1):
    g0: Circle CenterX=0 CenterY=0 CenterZ=0 NormalX=0 NormalY=0 NormalZ=1 AngleXU=0 Radius=12
  constraints (2):
    c: Coincident(g0,g-1)
    c: Diameter(g0) = 24
FEATURE [PartDesign::Pocket] Pocket004
  BaseFeature = -> Pad003
  Direction = (0,0,1)
  Length = 4.2
  Length2 = 5
  Profile = -> Sketch016
  ReferenceAxis = -> Sketch016 [N_Axis]
  Suppressed = false
  Type = 0
FEATURE [Sketcher::SketchObject] Sketch017
  ArcFitTolerance = 0
  AttachmentSupport = -> [Pocket004]
  FullyConstrained = true
  MakeInternals = false
  MapMode = 5
  Placement = pos=(0,0,4.2) rot=(1,0,0;3.14159rad)
  sketch-geometry (2):
    g0: Circle CenterX=0 CenterY=0 CenterZ=0 NormalX=0 NormalY=0 NormalZ=1 AngleXU=0 Radius=9.25
    g1: Circle CenterX=0 CenterY=0 CenterZ=0 NormalX=0 NormalY=0 NormalZ=1 AngleXU=0 Radius=6
  constraints (4):
    c: Coincident(g0,g-1)
    c: Diameter(g0) = 18.5
    c: Coincident(g1,g0)
    c: Diameter(g1) = 12
FEATURE [PartDesign::Pad] Pad004
  BaseFeature = -> Pocket004
  Direction = (0,0,-1)
  Length = 3.6
  Length2 = 10
  Profile = -> Sketch017
  ReferenceAxis = -> Sketch017 [N_Axis]
  Reversed = true
  Suppressed = false
  Type = 0
FEATURE [PartDesign::Body] Body
  AllowCompound = false
  Group = -> [Sketch,Pad,Sketch001,Pad001,Sketch002,Sketch003,AdditiveLoft,Sketch004,Pocket,Sketch005,Sketch006,SubtractiveLoft,Sketch007,Pocket001,Sketch008,Sketch009,SubtractiveLoft001,Sketch010,Pad002,Sketch011,Sketch012,AdditiveLoft001,MultiTransform,PolarPattern,LinearPattern,Sketch013,Pocket002,Sketch014,Pocket003,Sketch015,Pad003,Sketch016,Pocket004,Sketch017,Pad004]
  Origin = -> Origin
  Tip = -> Pad003
FEATURE [Mesh::Feature] Mesh  label="KnobStandard"
